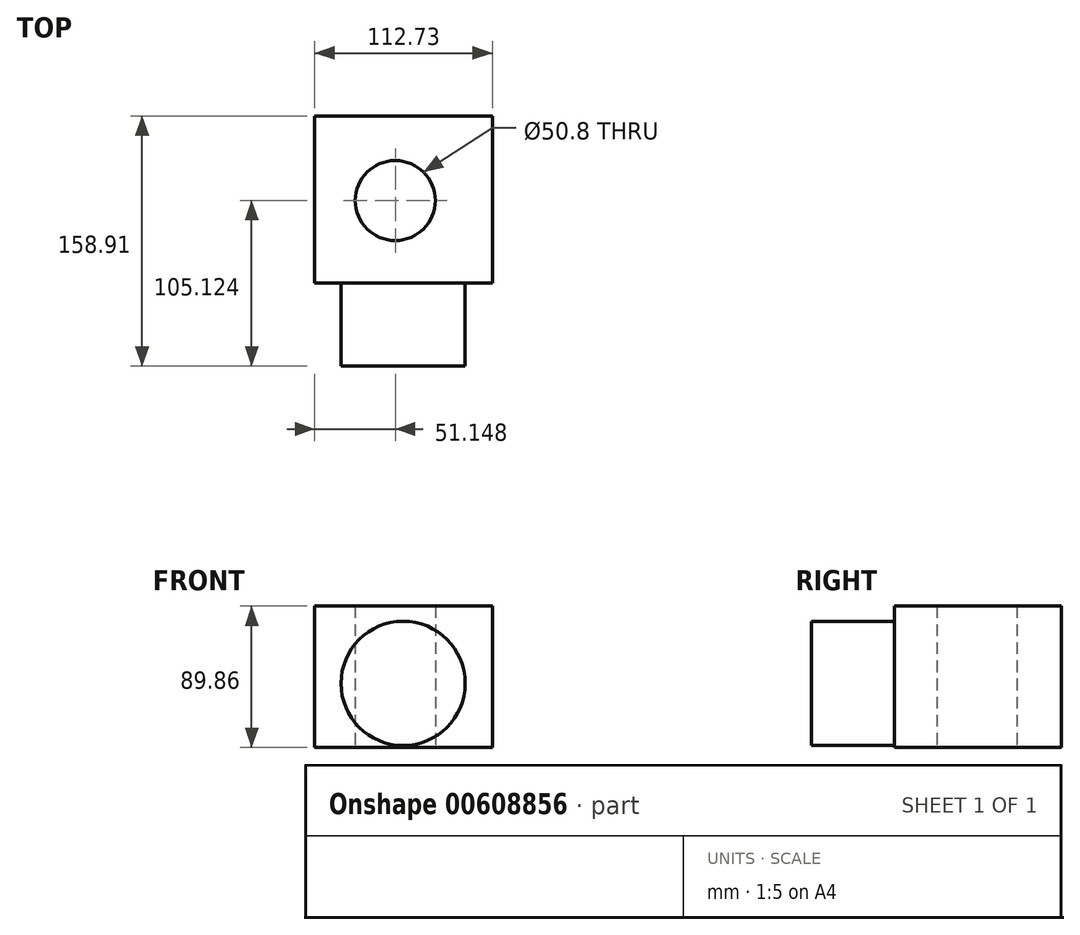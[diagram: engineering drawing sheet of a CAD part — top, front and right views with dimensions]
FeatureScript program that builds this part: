
annotation { "Feature Type Name" : "Feature", "Feature Type Description" : "" }
export const myFeature = defineFeature(function(context is Context, id is Id, definition is map)
    precondition{}
    {
        {
            var Q0;
            Q0=qCreatedBy(makeId("Top.planeOp"),FACE);
            var sketch = newSketch(context, id + "F0", { "sketchPlane" : qUnion([Q0])});
            skLineSegment(sketch, "E0.bottom", {"start": v(0, 0) * mm, "end": v(-112.73, 0) * mm});
            skLineSegment(sketch, "E0.top", {"start": v(0, -106.2) * mm, "end": v(-112.73, -106.2) * mm});
            skLineSegment(sketch, "E0.left", {"start": v(0, 0) * mm, "end": v(0, -106.2) * mm});
            skLineSegment(sketch, "E0.right", {"start": v(-112.73, 0) * mm, "end": v(-112.73, -106.2) * mm});
            skLineSegment(sketch, "E1.bottom", {"start": v(-56.36, -106.2) * mm, "end": v(-43.28, -106.2) * mm});
            skLineSegment(sketch, "E1.top", {"start": v(-56.36, -116.11) * mm, "end": v(-43.28, -116.11) * mm});
            skLineSegment(sketch, "E1.left", {"start": v(-56.36, -106.2) * mm, "end": v(-56.36, -116.11) * mm});
            skLineSegment(sketch, "E1.right", {"start": v(-43.28, -106.2) * mm, "end": v(-43.28, -116.11) * mm});
            skSolve(sketch);
        }
        {
            var Q0;
            Q0=makeQuery(id+"F0.imprint","IMPRINT",FACE,{"disambiguationData":[TD([[makeQuery(id+"F0.imprint","IMPRINT",EDGE,{"derivedFrom":sQuery(id+"F0.wireOp",EDGE,"E0.bottom")}),1.0]])]});
            var sketch = newSketch(context, id + "F1", { "sketchPlane" : qUnion([Q0])});
            skLineSegment(sketch, "E2.0", {"start": v(-112.73, 0) * mm, "end": v(-112.73, -106.2) * mm});
            skLineSegment(sketch, "E3.0", {"start": v(0, -106.2) * mm, "end": v(-112.73, -106.2) * mm});
            skSolve(sketch);
        }
        {
            var Q0;
            Q0=qSketchRegion(id+"F1",true);
            var Q1;
            Q1=makeQuery(id+"F0.imprint","IMPRINT",FACE,{"disambiguationData":[TD([[makeQuery(id+"F0.imprint","IMPRINT",EDGE,{"derivedFrom":sQuery(id+"F0.wireOp",EDGE,"E0.bottom")}),1.0]])]});
            extrude(context, id + "F2", {"entities" : qUnion([Q0, Q1]), "depth" : 89.86 * mm, "offsetDistance" : 25.4 * mm});
        }
        {
            var Q0;
            Q0=makeQuery(id+"F2.opExtrude","SWEPT_FACE",FACE,{"disambiguationData":[OSD([sQuery(id+"F0.wireOp",EDGE,"E0.bottom")])]});
            var sketch = newSketch(context, id + "F3", { "sketchPlane" : qUnion([Q0])});
            skCircle(sketch, "E4", {"center": v(56.62, 40.8) * mm, "radius": 39.44 * mm});
            skSolve(sketch);
        }
        {
            var Q0;
            Q0=makeQuery(id+"F3.imprint","IMPRINT",FACE,{"disambiguationData":[TD([[makeQuery(id+"F3.imprint","IMPRINT",EDGE,{"derivedFrom":sQuery(id+"F3.wireOp",EDGE,"E4")}),1.0]])]});
            extrude(context, id + "F4", {"entities" : qUnion([Q0]), "operationType" : NewBodyOperationType.ADD, "oppositeDirection" : true, "depth" : 158.9 * mm, "offsetDistance" : 25.4 * mm});
        }
        {
            var Q0;
            Q0=qCreatedBy(makeId("Top.planeOp"),FACE);
            var sketch = newSketch(context, id + "F5", { "sketchPlane" : qUnion([Q0])});
            skCircle(sketch, "E5", {"center": v(-61.58, -53.79) * mm, "radius": 35.92 * mm});
            skSolve(sketch);
        }
        {
            var Q0;
            Q0=sQuery(id+"F5.wireOp",VERTEX,"E5.center");
            var Q1;
            Q1=makeQuery(id+"F2.opExtrude","SWEPT_BODY",BODY,{"disambiguationData":[OSD([sQuery(id+"F0.wireOp",EDGE,"E0.bottom"),sQuery(id+"F0.wireOp",EDGE,"E0.top"),sQuery(id+"F0.wireOp",EDGE,"E0.left"),sQuery(id+"F0.wireOp",EDGE,"E0.right"),sQuery(id+"F0.wireOp",EDGE,"E1.bottom")])]});
            hole(context, id + "F6", {"style" : HoleStyle.SIMPLE, "endStyle" : HoleEndStyle.THROUGH, "oppositeDirection" : true, "holeDiameter" : 50.8 * mm, "majorDiameter" : 6.35 * mm, "isTappedThrough" : true, "tappedDepth" : 12.7 * mm, "tapClearance" : 3, "locations" : qUnion([Q0]), "scope" : qUnion([Q1])});
        }
    });
